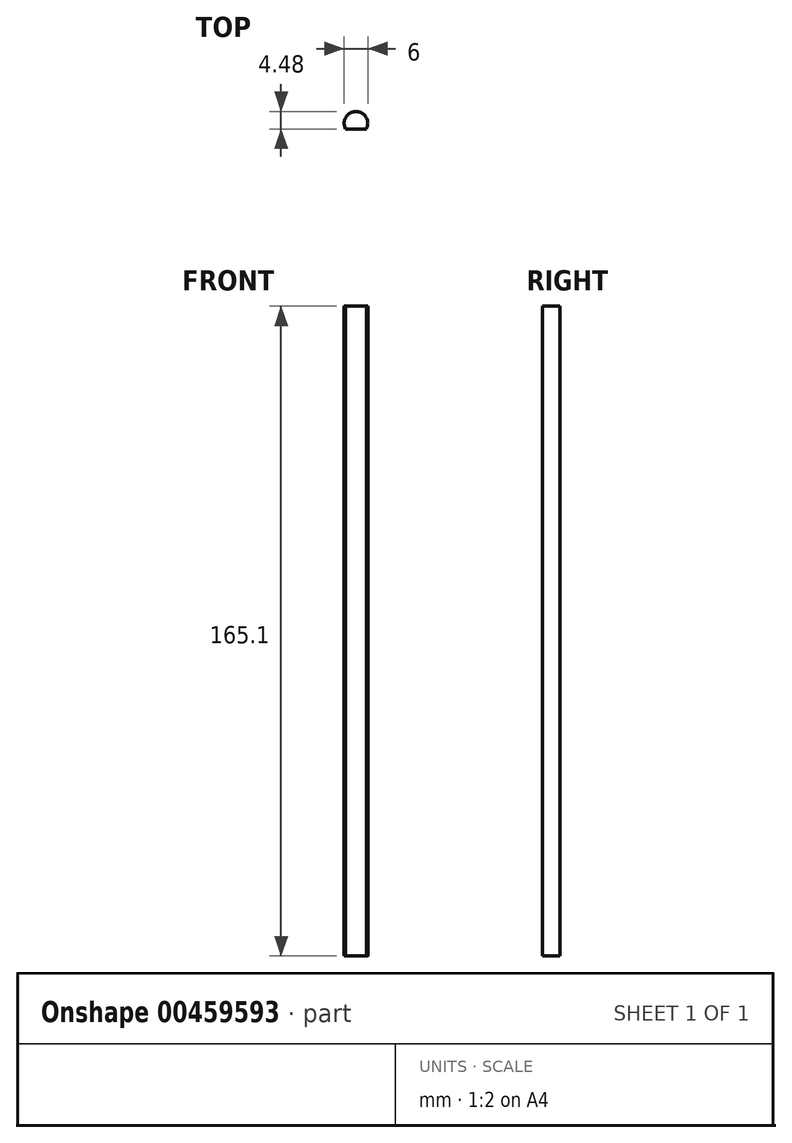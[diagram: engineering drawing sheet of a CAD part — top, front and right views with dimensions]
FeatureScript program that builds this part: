
annotation { "Feature Type Name" : "Feature", "Feature Type Description" : "" }
export const myFeature = defineFeature(function(context is Context, id is Id, definition is map)
    precondition{}
    {
        {
            var Q0;
            Q0=qCreatedBy(makeId("Top.planeOp"),FACE);
            var sketch = newSketch(context, id + "F0", { "sketchPlane" : qUnion([Q0])});
            skCircle(sketch, "E0", {"center": v(0, 0) * mm, "radius": 3 * mm});
            skSolve(sketch);
        }
        {
            var Q0;
            Q0=makeQuery(id+"F0.imprint","IMPRINT",FACE,{"disambiguationData":[TD([[makeQuery(id+"F0.imprint","IMPRINT",EDGE,{"derivedFrom":sQuery(id+"F0.wireOp",EDGE,"E0")}),1.0]])]});
            extrude(context, id + "F1", {"entities" : qUnion([Q0]), "depth" : 165.1 * mm});
        }
        {
            var Q0;
            Q0=makeQuery(id+"F1.opExtrude","CAP_FACE",FACE,{"disambiguationData":[OSD([sQuery(id+"F0.wireOp",EDGE,"E0")])],"isStart":false});
            var sketch = newSketch(context, id + "F2", { "sketchPlane" : qUnion([Q0])});
            skLineSegment(sketch, "E1.bottom", {"start": v(-4.72, -1.48) * mm, "end": v(14.88, -1.48) * mm});
            skLineSegment(sketch, "E1.top", {"start": v(-4.72, -7.46) * mm, "end": v(14.88, -7.46) * mm});
            skLineSegment(sketch, "E1.left", {"start": v(-4.72, -1.48) * mm, "end": v(-4.72, -7.46) * mm});
            skLineSegment(sketch, "E1.right", {"start": v(14.88, -1.48) * mm, "end": v(14.88, -7.46) * mm});
            skSolve(sketch);
        }
        {
            var Q0;
            Q0=makeQuery(id+"F2.imprint","IMPRINT",FACE,{"disambiguationData":[TD([[makeQuery(id+"F2.imprint","IMPRINT",EDGE,{"derivedFrom":sQuery(id+"F2.wireOp",EDGE,"E1.top")}),1.0]])]});
            var Q1;
            {var subQ0=sQuery(id+"F2.wireOp",EDGE,"E1.bottom");var subQ1=makeQuery(id+"F1.opExtrude","CAP_EDGE",EDGE,{"disambiguationData":[OSD([sQuery(id+"F0.wireOp",EDGE,"E0")])],"isStart":false});var subQ2=makeQuery(id+"F2.imprint","INTERSECT",VERTEX,{"disambiguationData":[OD(0.0)],"derivedFrom":[subQ1,subQ0]});Q1=makeQuery(id+"F2.imprint","IMPRINT",FACE,{"disambiguationData":[TD([[makeQuery(id+"F2.imprint","IMPRINT",EDGE,{"disambiguationData":[TD([[subQ2,-1.0]])],"derivedFrom":subQ0}),-1.0]])]});}
            extrude(context, id + "F3", {"entities" : qUnion([Q0, Q1]), "operationType" : NewBodyOperationType.REMOVE, "endBound" : BoundingType.THROUGH_ALL, "oppositeDirection" : true, "depth" : 25.4 * mm});
        }
    });
